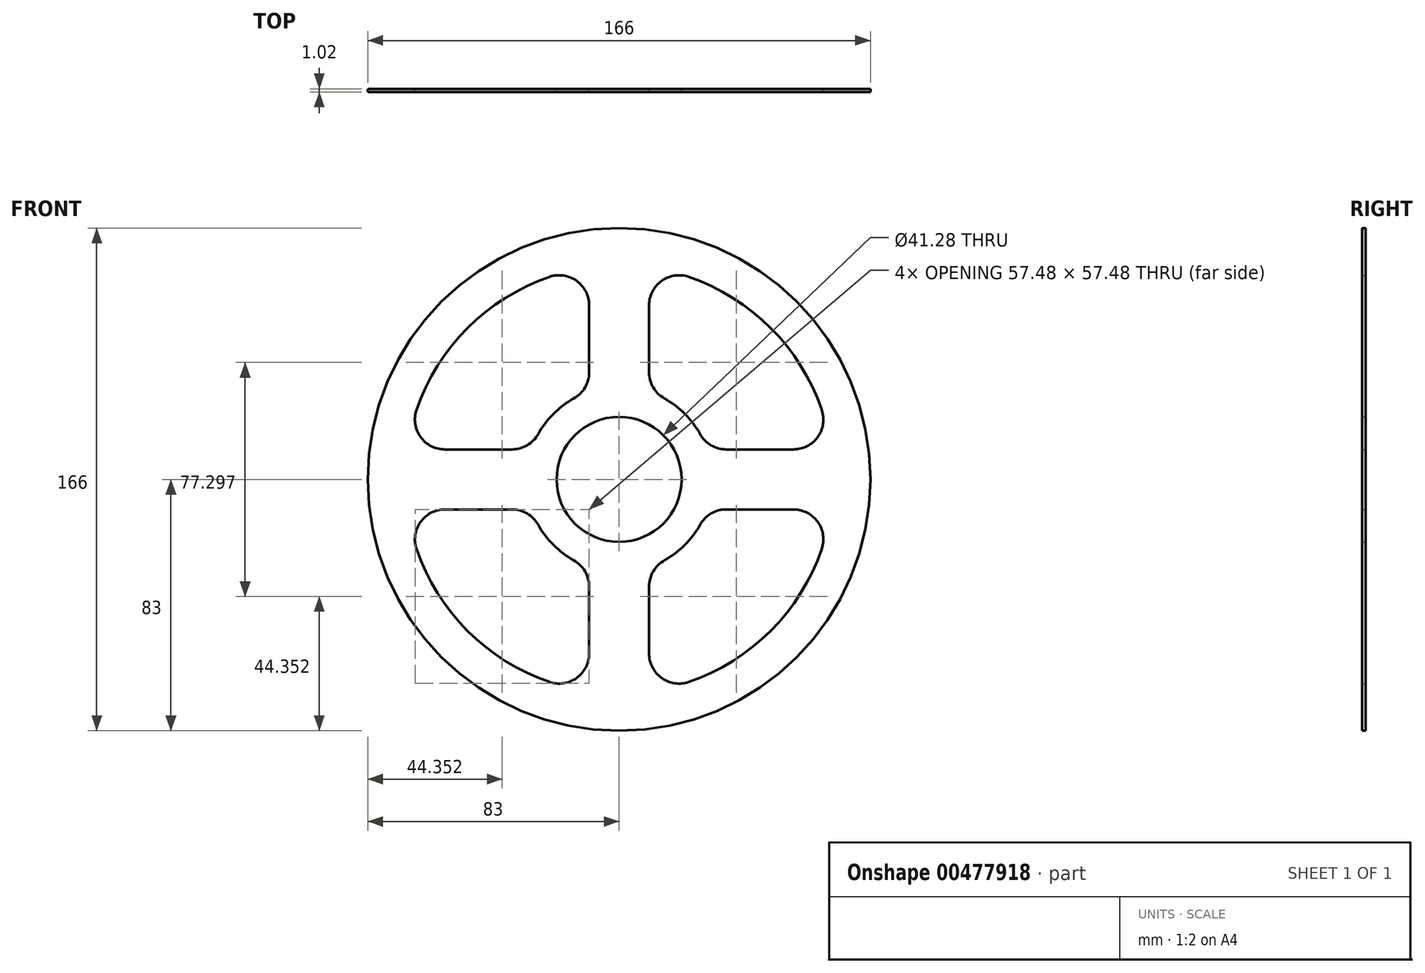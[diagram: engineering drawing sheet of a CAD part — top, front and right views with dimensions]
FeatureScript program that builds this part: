
annotation { "Feature Type Name" : "Feature", "Feature Type Description" : "" }
export const myFeature = defineFeature(function(context is Context, id is Id, definition is map)
    precondition{}
    {
        {
            var Q0;
            Q0=qCreatedBy(makeId("Front.planeOp"),FACE);
            var sketch = newSketch(context, id + "F0", { "sketchPlane" : qUnion([Q0])});
            skCircle(sketch, "E0", {"center": v(0, 0) * mm, "radius": 83 * mm});
            skCircle(sketch, "E1", {"center": v(0, 0) * mm, "radius": 20.64 * mm});
            skLineSegment(sketch, "E2", {"start": v(-87.13, 0) * mm, "end": v(0, 0) * mm, "construction": true});
            skLineSegment(sketch, "E3", {"start": v(0, 0) * mm, "end": v(0, 94.82) * mm, "construction": true});
            skLineSegment(sketch, "E4", {"start": v(-57.53, 9.9) * mm, "end": v(-35.38, 9.9) * mm});
            skLineSegment(sketch, "E5", {"start": v(-9.9, 35.38) * mm, "end": v(-9.9, 57.53) * mm});
            skArc(sketch, "E6", {"start": v(-66.9, 23.04) * mm, "mid": v(-50.03, 50.03) * mm, "end": v(-23.04, 66.9) * mm});
            skArc(sketch, "E7", {"start": v(-26.73, 14.97) * mm, "mid": v(-21.67, 21.67) * mm, "end": v(-14.97, 26.73) * mm});
            skPoint(sketch, "E8.visualSharp", {"position": v(-9.9, 70.05) * mm});
            skArc(sketch, "E8.filletArc", {"start": v(-9.9, 57.53) * mm, "mid": v(-14.06, 65.6) * mm, "end": v(-23.04, 66.9) * mm});
            skPoint(sketch, "E9.visualSharp", {"position": v(-70.05, 9.9) * mm});
            skArc(sketch, "E9.filletArc", {"start": v(-66.9, 23.04) * mm, "mid": v(-65.6, 14.06) * mm, "end": v(-57.53, 9.9) * mm});
            skPoint(sketch, "E10.visualSharp", {"position": v(-29, 9.9) * mm});
            skArc(sketch, "E10.filletArc", {"start": v(-35.38, 9.9) * mm, "mid": v(-30.37, 11.27) * mm, "end": v(-26.73, 14.97) * mm});
            skPoint(sketch, "E11.visualSharp", {"position": v(-9.9, 29) * mm});
            skArc(sketch, "E11.filletArc", {"start": v(-14.97, 26.73) * mm, "mid": v(-11.27, 30.37) * mm, "end": v(-9.9, 35.38) * mm});
            skArc(sketch, "E12.1.0", {"start": v(-23.04, -66.9) * mm, "mid": v(-50.03, -50.03) * mm, "end": v(-66.9, -23.04) * mm});
            skArc(sketch, "E12.1.1", {"start": v(-23.04, -66.9) * mm, "mid": v(-14.06, -65.6) * mm, "end": v(-9.9, -57.53) * mm});
            skLineSegment(sketch, "E12.1.2", {"start": v(-9.9, -57.53) * mm, "end": v(-9.9, -35.38) * mm});
            skArc(sketch, "E12.1.3", {"start": v(-9.9, -35.38) * mm, "mid": v(-11.27, -30.37) * mm, "end": v(-14.97, -26.73) * mm});
            skArc(sketch, "E12.1.4", {"start": v(-14.97, -26.73) * mm, "mid": v(-21.67, -21.67) * mm, "end": v(-26.73, -14.97) * mm});
            skArc(sketch, "E12.1.5", {"start": v(-26.73, -14.97) * mm, "mid": v(-30.37, -11.27) * mm, "end": v(-35.38, -9.9) * mm});
            skLineSegment(sketch, "E12.1.6", {"start": v(-35.38, -9.9) * mm, "end": v(-57.53, -9.9) * mm});
            skArc(sketch, "E12.1.7", {"start": v(-57.53, -9.9) * mm, "mid": v(-65.6, -14.06) * mm, "end": v(-66.9, -23.04) * mm});
            skArc(sketch, "E12.2.0", {"start": v(66.9, -23.04) * mm, "mid": v(50.03, -50.03) * mm, "end": v(23.04, -66.9) * mm});
            skArc(sketch, "E12.2.1", {"start": v(66.9, -23.04) * mm, "mid": v(65.6, -14.06) * mm, "end": v(57.53, -9.9) * mm});
            skLineSegment(sketch, "E12.2.2", {"start": v(57.53, -9.9) * mm, "end": v(35.38, -9.9) * mm});
            skArc(sketch, "E12.2.3", {"start": v(35.38, -9.9) * mm, "mid": v(30.37, -11.27) * mm, "end": v(26.73, -14.97) * mm});
            skArc(sketch, "E12.2.4", {"start": v(26.73, -14.97) * mm, "mid": v(21.67, -21.67) * mm, "end": v(14.97, -26.73) * mm});
            skArc(sketch, "E12.2.5", {"start": v(14.97, -26.73) * mm, "mid": v(11.27, -30.37) * mm, "end": v(9.9, -35.38) * mm});
            skLineSegment(sketch, "E12.2.6", {"start": v(9.9, -35.38) * mm, "end": v(9.9, -57.53) * mm});
            skArc(sketch, "E12.2.7", {"start": v(9.9, -57.53) * mm, "mid": v(14.06, -65.6) * mm, "end": v(23.04, -66.9) * mm});
            skArc(sketch, "E12.3.0", {"start": v(23.04, 66.9) * mm, "mid": v(50.03, 50.03) * mm, "end": v(66.9, 23.04) * mm});
            skArc(sketch, "E12.3.1", {"start": v(23.04, 66.9) * mm, "mid": v(14.06, 65.6) * mm, "end": v(9.9, 57.53) * mm});
            skLineSegment(sketch, "E12.3.2", {"start": v(9.9, 57.53) * mm, "end": v(9.9, 35.38) * mm});
            skArc(sketch, "E12.3.3", {"start": v(9.9, 35.38) * mm, "mid": v(11.27, 30.37) * mm, "end": v(14.97, 26.73) * mm});
            skArc(sketch, "E12.3.4", {"start": v(14.97, 26.73) * mm, "mid": v(21.67, 21.67) * mm, "end": v(26.73, 14.97) * mm});
            skArc(sketch, "E12.3.5", {"start": v(26.73, 14.97) * mm, "mid": v(30.37, 11.27) * mm, "end": v(35.38, 9.9) * mm});
            skLineSegment(sketch, "E12.3.6", {"start": v(35.38, 9.9) * mm, "end": v(57.53, 9.9) * mm});
            skArc(sketch, "E12.3.7", {"start": v(57.53, 9.9) * mm, "mid": v(65.6, 14.06) * mm, "end": v(66.9, 23.04) * mm});
            skSolve(sketch);
        }
        {
            var Q0;
            Q0=makeQuery(id+"F0.imprint","IMPRINT",FACE,{"disambiguationData":[TD([[makeQuery(id+"F0.imprint","IMPRINT",EDGE,{"derivedFrom":sQuery(id+"F0.wireOp",EDGE,"E0")}),1.0]])]});
            extrude(context, id + "F1", {"entities" : qUnion([Q0]), "depth" : 1.02 * mm});
        }
    });
